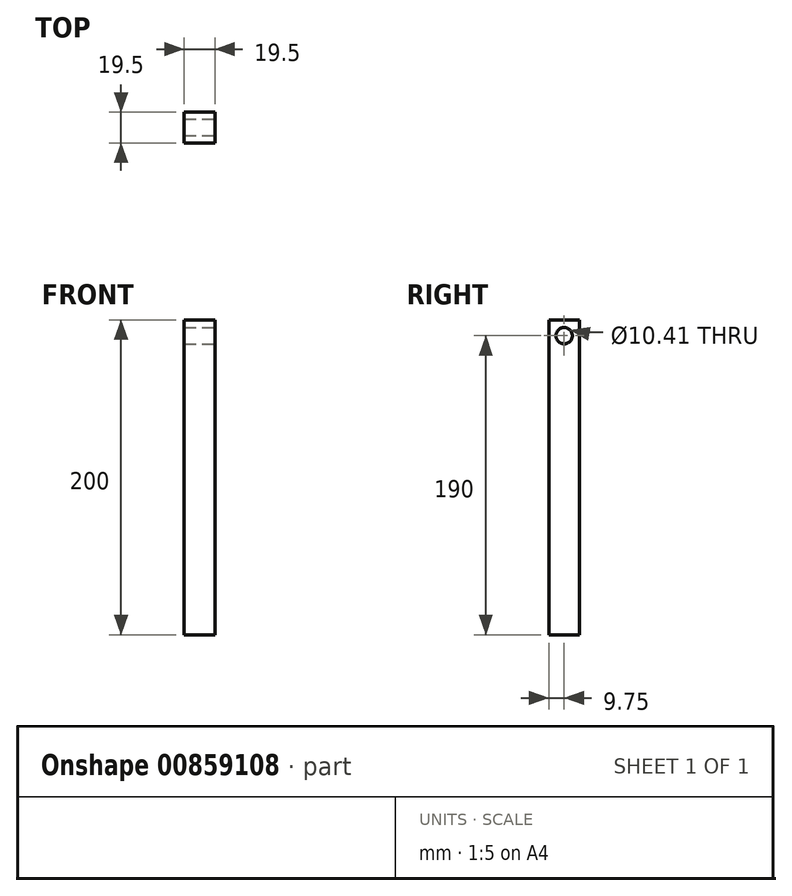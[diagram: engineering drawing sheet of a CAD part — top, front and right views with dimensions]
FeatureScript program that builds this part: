
annotation { "Feature Type Name" : "Feature", "Feature Type Description" : "" }
export const myFeature = defineFeature(function(context is Context, id is Id, definition is map)
    precondition{}
    {
        {
            var Q0;
            Q0=qCreatedBy(makeId("Front.planeOp"),FACE);
            var sketch = newSketch(context, id + "F0", { "sketchPlane" : qUnion([Q0])});
            skLineSegment(sketch, "E0.bottom", {"start": v(20, -50) * mm, "end": v(-20, -50) * mm});
            skLineSegment(sketch, "E0.top", {"start": v(20, 50) * mm, "end": v(-20, 50) * mm});
            skLineSegment(sketch, "E0.left", {"start": v(20, -50) * mm, "end": v(20, 50) * mm});
            skLineSegment(sketch, "E0.right", {"start": v(-20, -50) * mm, "end": v(-20, 50) * mm});
            skPoint(sketch, "E0.middle", {"position": v(0, 0) * mm});
            skSolve(sketch);
        }
        {
            var Q0;
            Q0=makeQuery(id+"F0.imprint","IMPRINT",FACE,{"disambiguationData":[TD([[makeQuery(id+"F0.imprint","IMPRINT",EDGE,{"derivedFrom":sQuery(id+"F0.wireOp",EDGE,"E0.bottom")}),-1.0]])]});
            extrude(context, id + "F1", {"entities" : qUnion([Q0]), "depth" : 40 * mm, "offsetDistance" : 25 * mm});
        }
        {
            var Q0;
            Q0=makeQuery(id+"F1.opExtrude","SWEPT_FACE",FACE,{"disambiguationData":[OSD([sQuery(id+"F0.wireOp",EDGE,"E0.top")])]});
            extrude(context, id + "F2", {"entities" : qUnion([Q0]), "operationType" : NewBodyOperationType.ADD, "depth" : 100 * mm, "offsetDistance" : 25 * mm});
        }
        {
            var Q0;
            {var subQ0=sQuery(id+"F0.wireOp",EDGE,"E0.left");Q0=makeQuery(id+"F2.boolean.opBoolean","MERGE",FACE,{"derivedFrom":[makeQuery(id+"F1.opExtrude","SWEPT_FACE",FACE,{"disambiguationData":[OSD([subQ0])]}),makeQuery(id+"F2.opExtrude","SWEPT_FACE",FACE,{"disambiguationData":[OSD([sQuery(id+"F0.wireOp",EDGE,"E0.top"),subQ0])]})]});}
            extrude(context, id + "F3", {"entities" : qUnion([Q0]), "operationType" : NewBodyOperationType.REMOVE, "oppositeDirection" : true, "depth" : 20.5 * mm, "offsetDistance" : 25 * mm});
        }
        {
            var Q0;
            {var subQ0=sQuery(id+"F0.wireOp",EDGE,"E0.top");Q0=makeQuery(id+"F2.boolean.opBoolean","MERGE",FACE,{"derivedFrom":[makeQuery(id+"F1.opExtrude","CAP_FACE",FACE,{"disambiguationData":[OSD([sQuery(id+"F0.wireOp",EDGE,"E0.bottom"),subQ0,sQuery(id+"F0.wireOp",EDGE,"E0.left"),sQuery(id+"F0.wireOp",EDGE,"E0.right")])],"isStart":false}),makeQuery(id+"F2.opExtrude","SWEPT_FACE",FACE,{"disambiguationData":[OSD([subQ0]),TDD([makeQuery(id+"F1.opExtrude","CAP_EDGE",EDGE,{"disambiguationData":[OSD([subQ0])],"isStart":false})])]})]});}
            extrude(context, id + "F4", {"entities" : qUnion([Q0]), "operationType" : NewBodyOperationType.REMOVE, "oppositeDirection" : true, "depth" : 20.5 * mm, "offsetDistance" : 25 * mm});
        }
        {
            var Q0;
            Q0=makeQuery(id+"F3.boolean.opBoolean","COPY",FACE,{"derivedFrom":makeQuery(id+"F3.opExtrude","CAP_FACE",FACE,{"disambiguationData":[OSD([sQuery(id+"F0.wireOp",EDGE,"E0.top"),sQuery(id+"F0.wireOp",EDGE,"E0.left")])],"isStart":false})});
            var sketch = newSketch(context, id + "F5", { "sketchPlane" : qUnion([Q0])});
            skLineSegment(sketch, "E1", {"start": v(-19.5, 150) * mm, "end": v(-19.5, 140) * mm});
            skLineSegment(sketch, "E2", {"start": v(-19.5, 140) * mm, "end": v(-9.75, 140) * mm});
            skCircle(sketch, "E3", {"center": v(-9.75, 140) * mm, "radius": 5.2 * mm});
            skSolve(sketch);
        }
        {
            var Q0;
            Q0=makeQuery(id+"F5.imprint","IMPRINT",FACE,{"disambiguationData":[TD([[makeQuery(id+"F5.imprint","IMPRINT",EDGE,{"derivedFrom":sQuery(id+"F5.wireOp",EDGE,"E3")}),1.0]])]});
            extrude(context, id + "F6", {"entities" : qUnion([Q0]), "operationType" : NewBodyOperationType.REMOVE, "oppositeDirection" : true, "depth" : 25 * mm, "offsetDistance" : 25 * mm});
        }
    });
